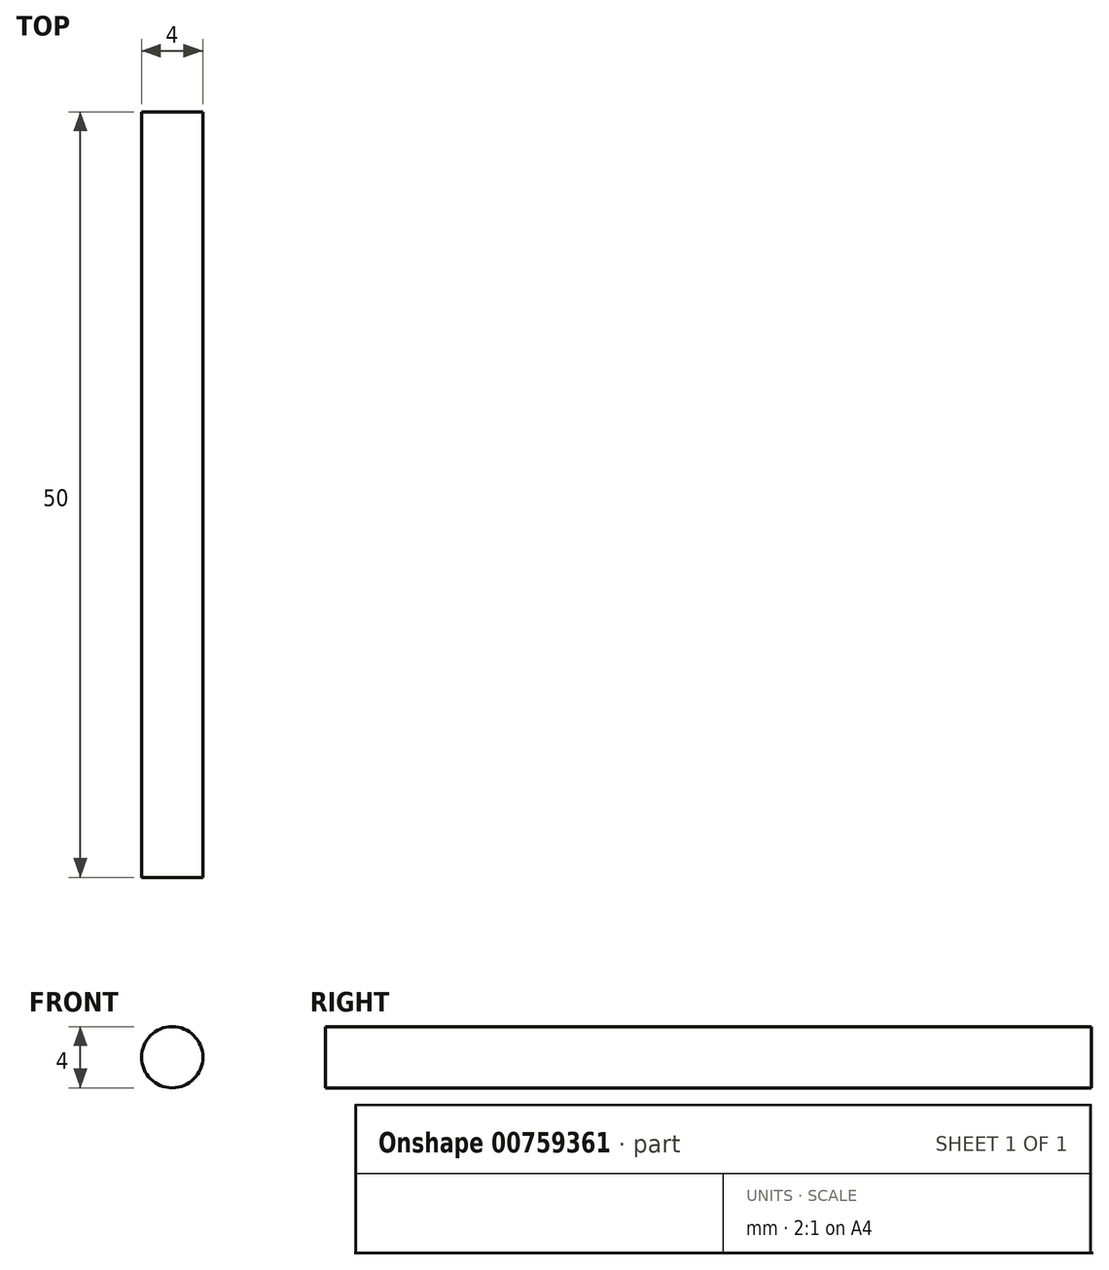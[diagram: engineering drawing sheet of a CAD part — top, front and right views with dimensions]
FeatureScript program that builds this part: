
annotation { "Feature Type Name" : "Feature", "Feature Type Description" : "" }
export const myFeature = defineFeature(function(context is Context, id is Id, definition is map)
    precondition{}
    {
        {
            var Q0;
            Q0=qCreatedBy(makeId("Front.planeOp"),FACE);
            var sketch = newSketch(context, id + "F0", { "sketchPlane" : qUnion([Q0])});
            skCircle(sketch, "E0", {"center": v(5.54, 2.72) * mm, "radius": 2 * mm});
            skSolve(sketch);
        }
        {
            var Q0;
            Q0 = qSketchRegion(id + "F0", true);
            extrude(context, id + "F1", {"entities" : qUnion([Q0]), "depth" : 50 * mm, "offsetDistance" : 25 * mm});
        }
    });
